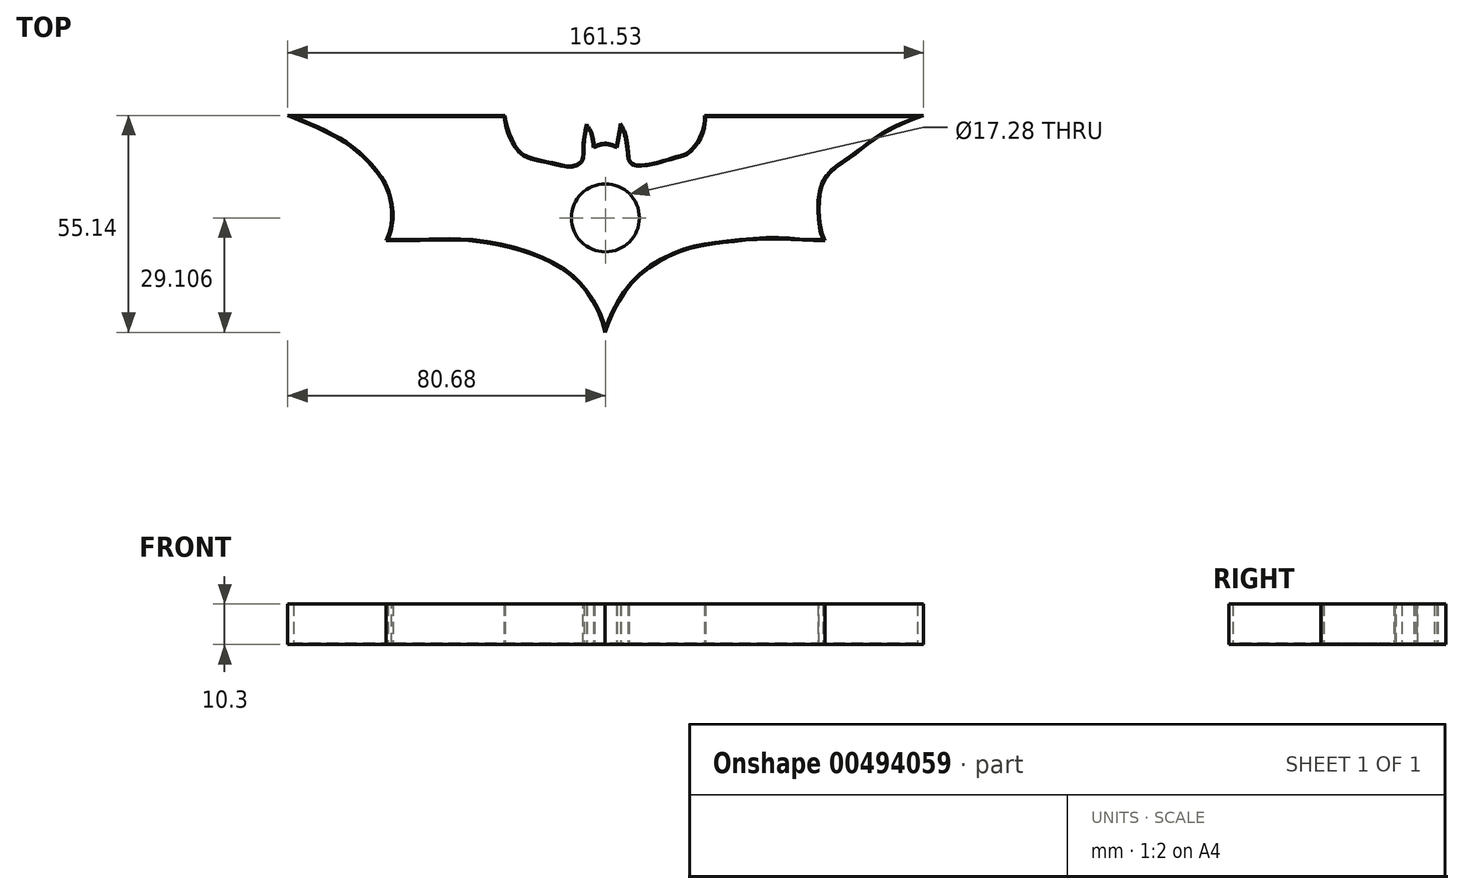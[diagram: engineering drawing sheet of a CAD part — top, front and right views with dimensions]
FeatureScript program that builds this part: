
annotation { "Feature Type Name" : "Feature", "Feature Type Description" : "" }
export const myFeature = defineFeature(function(context is Context, id is Id, definition is map)
    precondition{}
    {
        {
            var Q0;
            Q0=qCreatedBy(makeId("Top.planeOp"),FACE);
            var sketch = newSketch(context, id + "F0", { "sketchPlane" : qUnion([Q0])});
            skLineSegment(sketch, "E0", {"start": v(-79.18, 29.3) * mm, "end": v(-25.74, 29.3) * mm});
            skLineSegment(sketch, "E1", {"start": v(25.48, 29.32) * mm, "end": v(79.3, 29.32) * mm});
            skFitSpline(sketch, "E2", {"points": [v(-25.74, 29.3) * mm, v(-24.97, 25.8) * mm, v(-23.56, 22.58) * mm, v(-20.66, 19.28) * mm, v(-13.2, 17.24) * mm, v(-8.66, 16.46) * mm, v(-5.83, 17.87) * mm, v(-5.44, 21.4) * mm, v(-4.65, 26.66) * mm], "startDerivative": vector(5.48, -31.73) * mm, "endDerivative": vector(8.1, 39.14) * mm});
            skFitSpline(sketch, "E3", {"points": [v(-4.65, 26.66) * mm, v(-3.77, 25.17) * mm, v(-3.03, 21.4) * mm], "startDerivative": vector(2.4, -3.18) * mm, "endDerivative": vector(0.93, -7.08) * mm});
            skFitSpline(sketch, "E4", {"points": [v(-3.03, 21.4) * mm, v(0, 22.24) * mm, v(2.98, 21.4) * mm], "startDerivative": vector(6.06, 2.5) * mm, "endDerivative": vector(5.98, -2.52) * mm});
            skFitSpline(sketch, "E5", {"points": [v(2.98, 21.4) * mm, v(4.03, 26.66) * mm], "startDerivative": vector(1.05, 5.26) * mm, "endDerivative": vector(1.05, 5.26) * mm});
            skFitSpline(sketch, "E6", {"points": [v(4.03, 26.66) * mm, v(4.87, 24.65) * mm, v(5.76, 18.37) * mm], "startDerivative": vector(2.42, -4.6) * mm, "endDerivative": vector(1.14, -11.38) * mm});
            skFitSpline(sketch, "E7", {"points": [v(5.76, 18.37) * mm, v(7.07, 16.9) * mm, v(11.04, 16.95) * mm, v(15.07, 17.95) * mm, v(18.53, 18.94) * mm, v(20.78, 19.73) * mm, v(23.81, 23.08) * mm, v(25.28, 27.21) * mm, v(25.48, 29.32) * mm], "startDerivative": vector(10.12, -18.33) * mm, "endDerivative": vector(0.77, 19.35) * mm});
            skFitSpline(sketch, "E8", {"points": [v(79.3, 29.32) * mm, v(70.21, 25.09) * mm, v(62.2, 19.28) * mm, v(54.92, 12.14) * mm, v(54.63, 0) * mm, v(55.3, -1.85) * mm], "startDerivative": vector(-42.82, -17.16) * mm, "endDerivative": vector(6.75, -13.28) * mm});
            skFitSpline(sketch, "E9", {"points": [v(55.3, -1.85) * mm, v(50.89, -1.85) * mm, v(42.67, -1.44) * mm, v(29.57, -2.44) * mm, v(20.87, -4.07) * mm, v(10.28, -9.33) * mm, v(2.98, -17.84) * mm, v(0, -24.56) * mm], "startDerivative": vector(-41.66, -1.13) * mm, "endDerivative": vector(-19.05, -50.88) * mm});
            skFitSpline(sketch, "E10", {"points": [v(0, -24.56) * mm, v(-1.59, -19.98) * mm, v(-6.47, -12.8) * mm, v(-17.2, -5.84) * mm, v(-35.04, -1.85) * mm, v(-45.55, -1.85) * mm, v(-55.27, -1.85) * mm], "startDerivative": vector(-10.86, 38.37) * mm, "endDerivative": vector(-61.11, 0.82) * mm});
            skFitSpline(sketch, "E11", {"points": [v(-55.27, -1.85) * mm, v(-54.3, 0.79) * mm, v(-54.17, 7) * mm, v(-56.73, 13.81) * mm, v(-63.17, 20.83) * mm, v(-69.87, 25.17) * mm, v(-79.18, 29.3) * mm], "startDerivative": vector(10.4, 21.98) * mm, "endDerivative": vector(-49, 20.4) * mm});
            skSolve(sketch);
        }
        {
            var Q0;
            Q0=makeQuery(id+"F0.imprint","IMPRINT",FACE,{"disambiguationData":[TD([[makeQuery(id+"F0.imprint","IMPRINT",EDGE,{"derivedFrom":sQuery(id+"F0.wireOp",EDGE,"E0")}),-1.0]])]});
            extrude(context, id + "F1", {"entities" : qUnion([Q0]), "depth" : 10 * mm});
        }
        {
            var Q0;
            Q0=makeQuery(id+"F1.opExtrude","CAP_FACE",FACE,{"disambiguationData":[OSD([sQuery(id+"F0.wireOp",EDGE,"E0"),sQuery(id+"F0.wireOp",EDGE,"E1"),sQuery(id+"F0.wireOp",EDGE,"E2"),sQuery(id+"F0.wireOp",EDGE,"E3"),sQuery(id+"F0.wireOp",EDGE,"E4"),sQuery(id+"F0.wireOp",EDGE,"E5"),sQuery(id+"F0.wireOp",EDGE,"E6"),sQuery(id+"F0.wireOp",EDGE,"E7"),sQuery(id+"F0.wireOp",EDGE,"E8"),sQuery(id+"F0.wireOp",EDGE,"E9"),sQuery(id+"F0.wireOp",EDGE,"E10"),sQuery(id+"F0.wireOp",EDGE,"E11")])],"isStart":false});
            shell(context, id + "F2", {"entities" : qUnion([Q0]), "thickness" : .3 * mm, "oppositeDirection" : true});
        }
        {
            var Q0;
            Q0=makeQuery(id+"F2.opShell","OFFSET_FACE",FACE,{"disambiguationData":[OSD([sQuery(id+"F0.wireOp",EDGE,"E0"),sQuery(id+"F0.wireOp",EDGE,"E1"),sQuery(id+"F0.wireOp",EDGE,"E2"),sQuery(id+"F0.wireOp",EDGE,"E3"),sQuery(id+"F0.wireOp",EDGE,"E4"),sQuery(id+"F0.wireOp",EDGE,"E5"),sQuery(id+"F0.wireOp",EDGE,"E6"),sQuery(id+"F0.wireOp",EDGE,"E7"),sQuery(id+"F0.wireOp",EDGE,"E8"),sQuery(id+"F0.wireOp",EDGE,"E9"),sQuery(id+"F0.wireOp",EDGE,"E10"),sQuery(id+"F0.wireOp",EDGE,"E11")])]});
            var sketch = newSketch(context, id + "F3", { "sketchPlane" : qUnion([Q0])});
            skCircle(sketch, "E12", {"center": v(0, 3.59) * mm, "radius": 8.64 * mm});
            skSolve(sketch);
        }
        {
            var Q0;
            Q0 = qSketchRegion(id + "F3", true);
            extrude(context, id + "F4", {"entities" : qUnion([Q0]), "operationType" : NewBodyOperationType.REMOVE, "oppositeDirection" : true, "depth" : 25.4 * mm});
        }
    });
